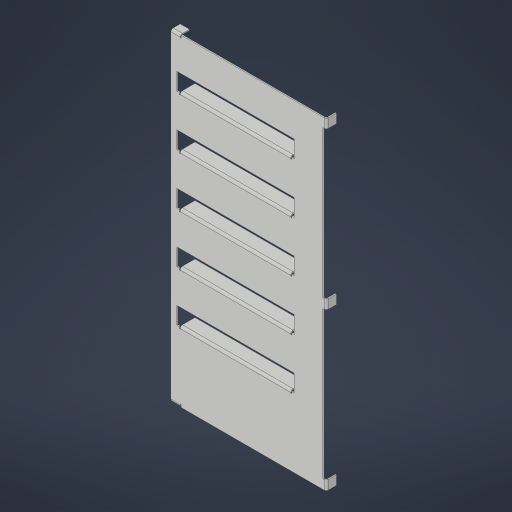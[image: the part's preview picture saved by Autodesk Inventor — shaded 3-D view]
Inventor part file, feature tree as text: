
AUTODESK INVENTOR PART (.ipt)
format: ipt  version: 2023.4 (Build 274418000, 418)  size: 552,960 bytes
history: native  units: in
note: dims shown in document units (in); Inventor stores cm internally (conversion verified against a paired STEP export)
features: sheet_metal_op x12, sketch x7, other x6, extrude x2, projected_geometry x2, pattern_linear x1
ambient origin geometry x8: Origin, YZ Plane, XZ Plane, XY Plane, X Axis, Y Axis, Z Axis, Center Point
bodies: Solid1 (feature_tree)
feature tree (30):
  sheet_metal_op  "Face1"
  sketch  "Sketch2"  dims[d1=35.0in]
  sheet_metal_op  "Face2"
  sheet_metal_op  "Fold1"
  sheet_metal_op  "Fold2"
  sketch  "Sketch3"  dims[d2=0.12in]
  sheet_metal_op  "Fold4"
  pattern_linear  "Rectangular Pattern1"  Spacing1=1.0in  [1 undecoded]
  extrude  "Extrusion1"  Depth=1.5in
  sheet_metal_op  "Flange1"
  sheet_metal_op  "Flange2"
  extrude  "Extrusion2"  Depth=1.0in
  sketch  "Sketch1"  dims[d0=16.5in]
  other  "Plate1"
  other  "Plate2"
  sheet_metal_op  "Bend1"
  sketch  "Sketch4"  dims[d3=1.25in]
  sketch  "Sketch5"  dims[d4=1.0in]
  other  "Plate3"
  sheet_metal_op  "Bend2"
  sheet_metal_op  "Corner1"
  sketch  "Sketch6"  dims[d5=0.25in]
  other  "Plate4"
  sheet_metal_op  "Bend3"
  sheet_metal_op  "Corner2"
  sketch  "Sketch7"  dims[d6=1.0in d7=1.0in d8=1.25in d9=1.0in d10=0.25in d11=0.12in d12=0.12in d13=0.06in d14=0.24in d15=0.12in d16=0.12in d17=0.06in d18=0.24in d19=0.12in d20=90.0deg d21=0.12in d22=0.12in d23=0.06in d24=0.24in d25=0.12in d26=90.0deg d27=0.12in d28=5.5in d29=1.5in d30=12.0in d31=1.0in d32=0.375in d33=0.12in d34=0.0in d41=0.12in d42=0.06in d43=0.24in d44=0.12in d45=90.0deg d46=0.12in d47=1.9685in d49=5.5in d50=1.0in d51=0.0in d52=0.12in d53=0.06in d54=0.24in d55=0.12in d56=1.0in d57=0.0in d58=1.0in d59=90.0deg d60=0.12in d61=0.48in d62=0.12in d63=0.12in d64=0.12in d65=0.06in d66=0.24in d67=0.12in d68=1.0in d69=0.0in d70=1.0in d71=90.0deg d72=0.12in d73=0.48in d74=0.12in d75=0.12in d76=11.31in d77=1.5in d78=4.45in d79=1.5in d80=5.35in d81=4.45in d82=0.0in d83=0.0in]
  other  "Cut1"
  projected_geometry  "Project Cut Edges1"
  projected_geometry  "Project Cut Edges2"
  other  "Definition1"
note: 1 required parameter value undecoded (feature->parameter linkage not recoverable at this tier; creation-order binding heuristic only, values carry confidence <= 0.55)
